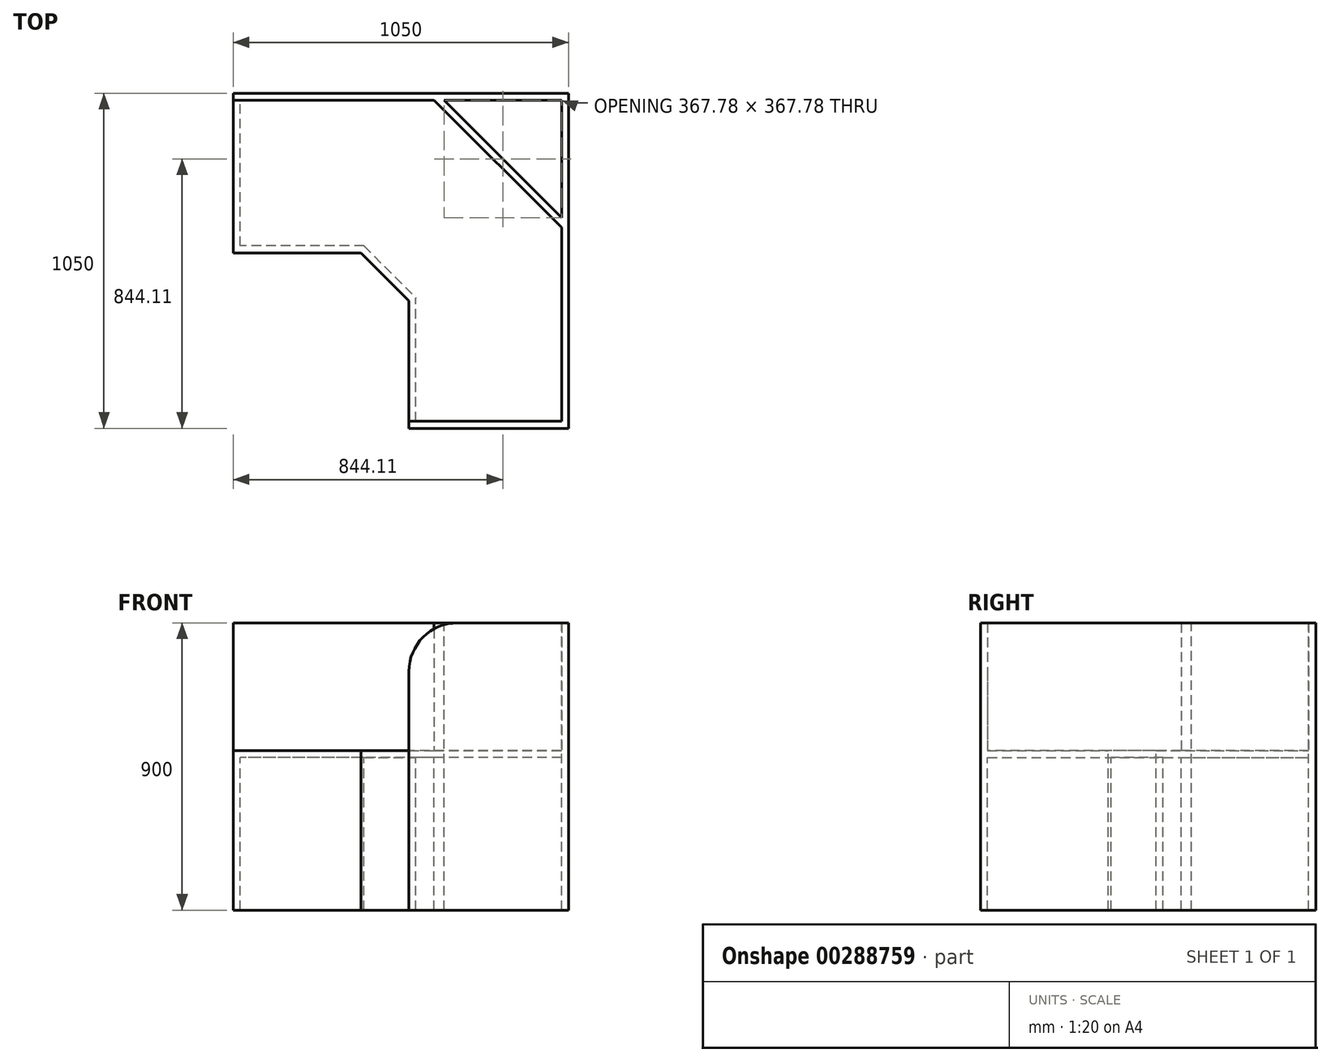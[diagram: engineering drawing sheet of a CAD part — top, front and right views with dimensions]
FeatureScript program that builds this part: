
annotation { "Feature Type Name" : "Feature", "Feature Type Description" : "" }
export const myFeature = defineFeature(function(context is Context, id is Id, definition is map)
    precondition{}
    {
        {
            var Q0;
            Q0=qCreatedBy(makeId("Top.planeOp"),FACE);
            var sketch = newSketch(context, id + "F0", { "sketchPlane" : qUnion([Q0])});
            skLineSegment(sketch, "E0", {"start": v(-1050, 0) * mm, "end": v(0, 0) * mm});
            skLineSegment(sketch, "E1", {"start": v(0, 0) * mm, "end": v(0, -1050) * mm});
            skLineSegment(sketch, "E2", {"start": v(0, -1050) * mm, "end": v(-500, -1050) * mm});
            skLineSegment(sketch, "E3", {"start": v(-500, -1050) * mm, "end": v(-500, -650) * mm});
            skLineSegment(sketch, "E4", {"start": v(-650, -500) * mm, "end": v(-1050, -500) * mm});
            skLineSegment(sketch, "E5", {"start": v(-1050, -500) * mm, "end": v(-1050, 0) * mm});
            skLineSegment(sketch, "E6", {"start": v(-650, -500) * mm, "end": v(-500, -650) * mm});
            skLineSegment(sketch, "E7", {"start": v(-1050, -22) * mm, "end": v(-420.9, -22) * mm});
            skLineSegment(sketch, "E8", {"start": v(-22, -22) * mm, "end": v(-22, -389.78) * mm});
            skLineSegment(sketch, "E9", {"start": v(-420.9, -22) * mm, "end": v(-22, -420.9) * mm});
            skLineSegment(sketch, "E10", {"start": v(-389.78, -22) * mm, "end": v(-22, -389.78) * mm});
            skLineSegment(sketch, "E11.trimOffspring", {"start": v(-22, -420.9) * mm, "end": v(-22, -1028) * mm});
            skLineSegment(sketch, "E12.trimOffspring", {"start": v(-389.78, -22) * mm, "end": v(-22, -22) * mm});
            skLineSegment(sketch, "E13", {"start": v(-22, -420.9) * mm, "end": v(0, -420.9) * mm, "construction": true});
            skLineSegment(sketch, "E14", {"start": v(-420.9, -22) * mm, "end": v(-420.9, 0) * mm, "construction": true});
            skLineSegment(sketch, "E15", {"start": v(-221.45, -221.45) * mm, "end": v(-205.9, -205.9) * mm, "construction": true});
            skLineSegment(sketch, "E16", {"start": v(-575, -575) * mm, "end": v(-221.45, -221.45) * mm, "construction": true});
            skLineSegment(sketch, "E17", {"start": v(-22, -1028) * mm, "end": v(-500, -1028) * mm});
            skLineSegment(sketch, "E18", {"start": v(-250, -1028) * mm, "end": v(-250, -1050) * mm, "construction": true});
            skSolve(sketch);
        }
        {
            var Q0;
            {var subQ3=sQuery(id+"F0.wireOp",EDGE,"E3");Q0=makeQuery(id+"F0.imprint","IMPRINT",FACE,{"disambiguationData":[TD([[makeQuery(id+"F0.imprint","IMPRINT",EDGE,{"derivedFrom":subQ3}),-1.0]])]});}
            var Q1;
            {var subQ1=sQuery(id+"F0.wireOp",EDGE,"E0");Q1=makeQuery(id+"F0.imprint","IMPRINT",FACE,{"disambiguationData":[TD([[makeQuery(id+"F0.imprint","IMPRINT",EDGE,{"derivedFrom":subQ1}),-1.0]])]});}
            extrude(context, id + "F1", {"entities" : qUnion([Q0, Q1]), "oppositeDirection" : true, "depth" : 500 * mm});
        }
        {
            var Q0;
            {var subQ1=sQuery(id+"F0.wireOp",EDGE,"E0");Q0=makeQuery(id+"F0.imprint","IMPRINT",FACE,{"disambiguationData":[TD([[makeQuery(id+"F0.imprint","IMPRINT",EDGE,{"derivedFrom":subQ1}),-1.0]])]});}
            extrude(context, id + "F2", {"entities" : qUnion([Q0]), "operationType" : NewBodyOperationType.ADD, "depth" : 400 * mm});
        }
        {
            var Q0;
            Q0=makeQuery(id+"F1.opExtrude","CAP_FACE",FACE,{"disambiguationData":[OSD([sQuery(id+"F0.wireOp",EDGE,"E0"),sQuery(id+"F0.wireOp",EDGE,"E1"),sQuery(id+"F0.wireOp",EDGE,"E2"),sQuery(id+"F0.wireOp",EDGE,"E3"),sQuery(id+"F0.wireOp",EDGE,"E4"),sQuery(id+"F0.wireOp",EDGE,"E5"),sQuery(id+"F0.wireOp",EDGE,"E6"),sQuery(id+"F0.wireOp",EDGE,"E8"),sQuery(id+"F0.wireOp",EDGE,"E10"),sQuery(id+"F0.wireOp",EDGE,"E12.trimOffspring")])],"isStart":false});
            shell(context, id + "F3", {"entities" : qUnion([Q0]), "thickness" : 22 * mm});
        }
        {
            var Q0;
            {var subQ0=sQuery(id+"F0.wireOp",EDGE,"E2");Q0=makeQuery(id+"F2.boolean.opBoolean","MERGE",FACE,{"derivedFrom":[makeQuery(id+"F1.opExtrude","SWEPT_FACE",FACE,{"disambiguationData":[OSD([subQ0])]}),makeQuery(id+"F2.opExtrude","SWEPT_FACE",FACE,{"disambiguationData":[OSD([subQ0])]})]});}
            var sketch = newSketch(context, id + "F4", { "sketchPlane" : qUnion([Q0])});
            skPoint(sketch, "E19.visualSharp", {"position": v(-500, 400) * mm});
            skArc(sketch, "E19.filletArc", {"start": v(-348, 400) * mm, "mid": v(-455.48, 355.48) * mm, "end": v(-500, 248) * mm});
            skLineSegment(sketch, "E20", {"start": v(-348, 400) * mm, "end": v(-500, 400) * mm});
            skLineSegment(sketch, "E21", {"start": v(-500, 248) * mm, "end": v(-500, 400) * mm});
            skSolve(sketch);
        }
        {
            var Q0;
            Q0 = qSketchRegion(id + "F4", true);
            extrude(context, id + "F5", {"entities" : qUnion([Q0]), "operationType" : NewBodyOperationType.REMOVE, "oppositeDirection" : true, "depth" : 25 * mm});
        }
    });
